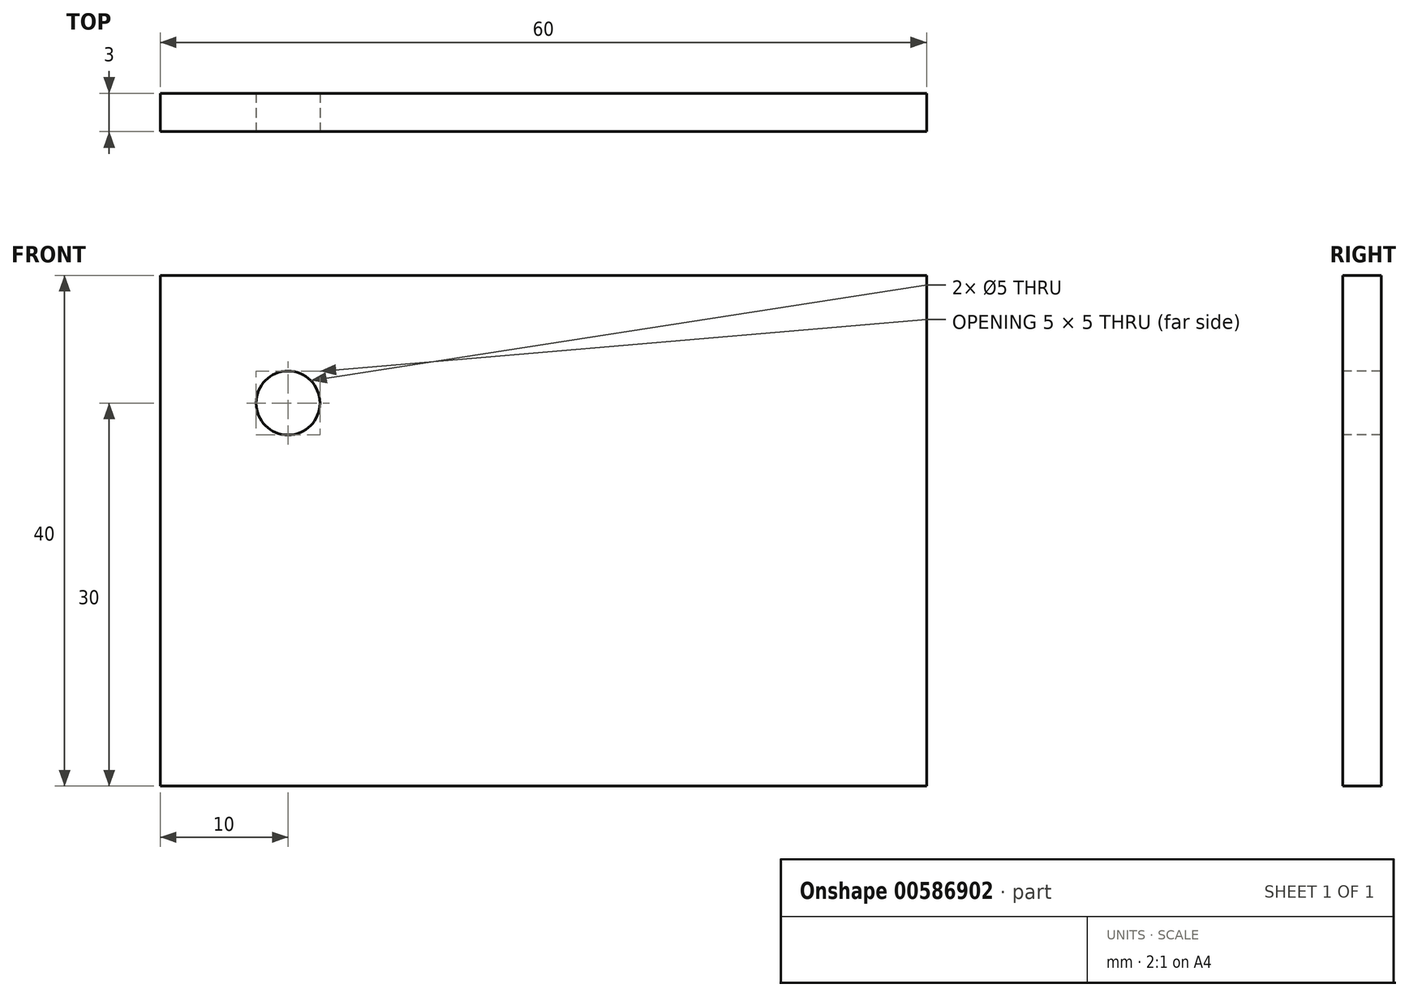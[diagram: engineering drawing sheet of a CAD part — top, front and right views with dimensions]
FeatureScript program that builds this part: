
annotation { "Feature Type Name" : "Feature", "Feature Type Description" : "" }
export const myFeature = defineFeature(function(context is Context, id is Id, definition is map)
    precondition{}
    {
        {
            var Q0;
            Q0=qCreatedBy(makeId("Top.planeOp"),FACE);
            var sketch = newSketch(context, id + "F0", { "sketchPlane" : qUnion([Q0])});
            skLineSegment(sketch, "E0.bottom", {"start": v(0, 0) * mm, "end": v(60, 0) * mm});
            skLineSegment(sketch, "E0.top", {"start": v(0, 3) * mm, "end": v(60, 3) * mm});
            skLineSegment(sketch, "E0.left", {"start": v(0, 0) * mm, "end": v(0, 3) * mm});
            skLineSegment(sketch, "E0.right", {"start": v(60, 0) * mm, "end": v(60, 3) * mm});
            skSolve(sketch);
        }
        {
            var Q0;
            Q0=makeQuery(id+"F0.imprint","IMPRINT",FACE,{"disambiguationData":[TD([[makeQuery(id+"F0.imprint","IMPRINT",EDGE,{"derivedFrom":sQuery(id+"F0.wireOp",EDGE,"E0.bottom")}),1.0]])]});
            extrude(context, id + "F1", {"entities" : qUnion([Q0]), "depth" : 40 * mm, "offsetDistance" : 25 * mm});
        }
        {
            var Q0;
            Q0=makeQuery(id+"F1.opExtrude","SWEPT_FACE",FACE,{"disambiguationData":[OSD([sQuery(id+"F0.wireOp",EDGE,"E0.bottom")])]});
            var sketch = newSketch(context, id + "F2", { "sketchPlane" : qUnion([Q0])});
            skCircle(sketch, "E1", {"center": v(10, 30) * mm, "radius": 2.5 * mm});
            skSolve(sketch);
        }
        {
            var Q0;
            Q0=sQuery(id+"F2.wireOp",VERTEX,"E1.center");
            var Q1;
            Q1=makeQuery(id+"F1.opExtrude","SWEPT_BODY",BODY,{"disambiguationData":[OSD([sQuery(id+"F0.wireOp",EDGE,"E0.bottom"),sQuery(id+"F0.wireOp",EDGE,"E0.top"),sQuery(id+"F0.wireOp",EDGE,"E0.left"),sQuery(id+"F0.wireOp",EDGE,"E0.right")])]});
            hole(context, id + "F3", {"style" : HoleStyle.SIMPLE, "endStyle" : HoleEndStyle.THROUGH, "holeDiameter" : 5 * mm, "majorDiameter" : 5 * mm, "isTappedThrough" : true, "tappedDepth" : 12 * mm, "tapClearance" : 3, "locations" : qUnion([Q0]), "scope" : qUnion([Q1])});
        }
        {
            var Q0;
            Q0=makeQuery(id+"F1.opExtrude","SWEPT_BODY",BODY,{"disambiguationData":[OSD([sQuery(id+"F0.wireOp",EDGE,"E0.bottom"),sQuery(id+"F0.wireOp",EDGE,"E0.top"),sQuery(id+"F0.wireOp",EDGE,"E0.left"),sQuery(id+"F0.wireOp",EDGE,"E0.right")])]});
            transform(context, id + "F4", {"entities" : qUnion([Q0]), "transformType" : TransformType.TRANSLATION_3D, "dx" : 0 * mm, "dy" : 0 * mm, "dz" : 0 * mm, "makeCopy" : true});
        }
    });
